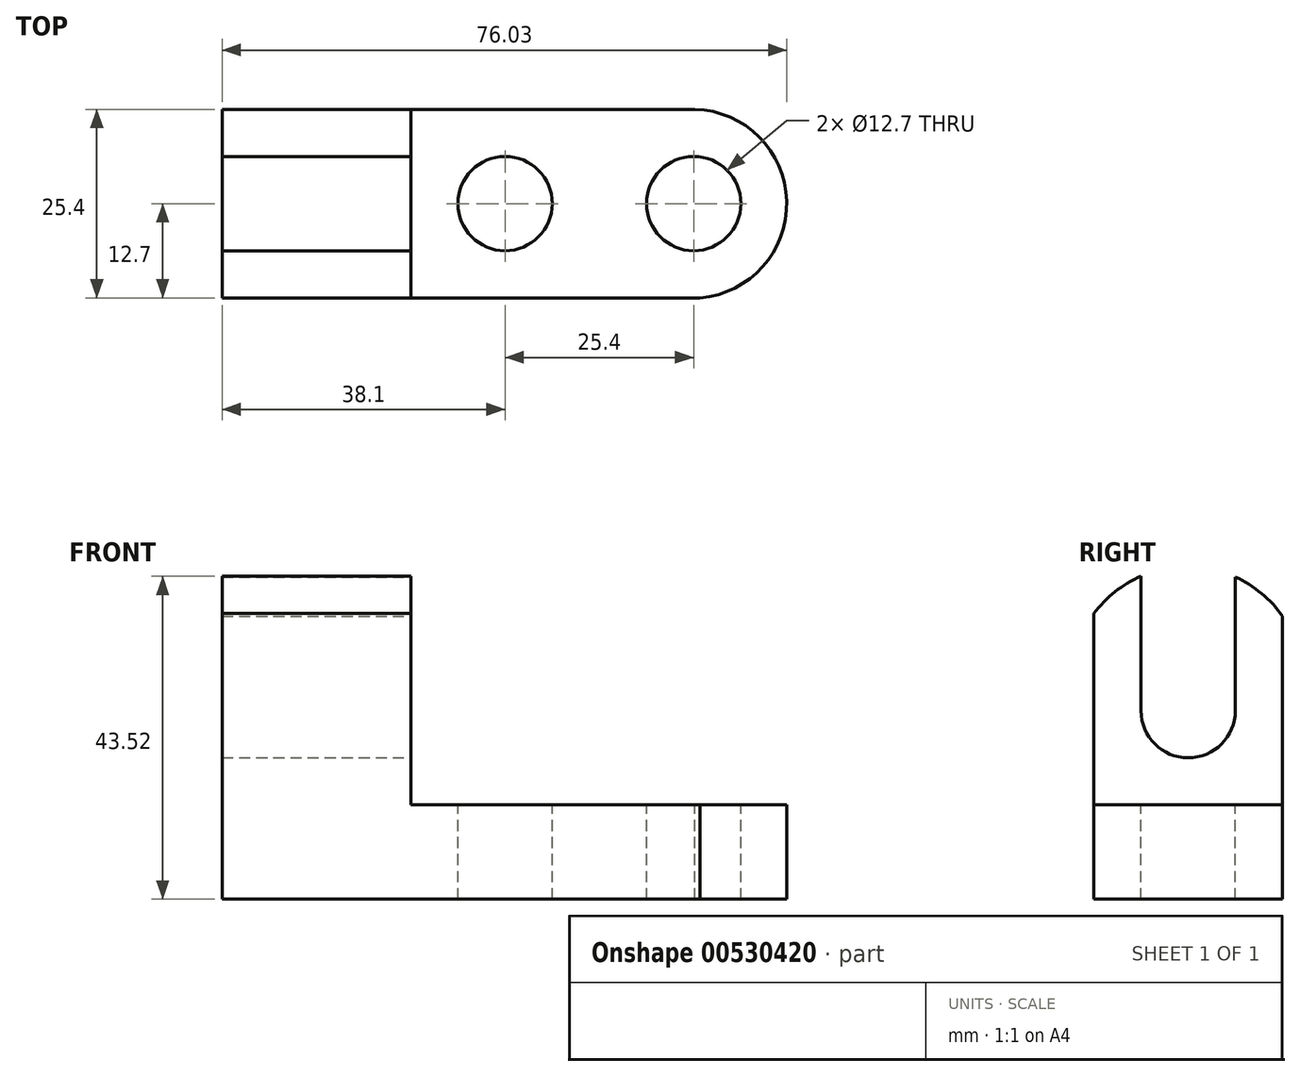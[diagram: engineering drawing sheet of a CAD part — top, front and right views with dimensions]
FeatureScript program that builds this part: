
annotation { "Feature Type Name" : "Feature", "Feature Type Description" : "" }
export const myFeature = defineFeature(function(context is Context, id is Id, definition is map)
    precondition{}
    {
        {
            var Q0;
            Q0=qCreatedBy(makeId("Front.planeOp"),FACE);
            var sketch = newSketch(context, id + "F0", { "sketchPlane" : qUnion([Q0])});
            skLineSegment(sketch, "E0", {"start": v(-76.2, 44.45) * mm, "end": v(-76.2, 0) * mm});
            skLineSegment(sketch, "E1", {"start": v(-76.2, 0) * mm, "end": v(0, 0) * mm});
            skLineSegment(sketch, "E2", {"start": v(-76.2, 44.45) * mm, "end": v(-50.8, 44.45) * mm});
            skLineSegment(sketch, "E3", {"start": v(-50.8, 44.45) * mm, "end": v(-50.8, 12.7) * mm});
            skLineSegment(sketch, "E4", {"start": v(-50.8, 12.7) * mm, "end": v(0, 12.7) * mm});
            skLineSegment(sketch, "E5", {"start": v(0, 12.7) * mm, "end": v(0, 0) * mm});
            skSolve(sketch);
        }
        {
            var Q0;
            Q0=makeQuery(id+"F0.imprint","IMPRINT",FACE,{"disambiguationData":[TD([[makeQuery(id+"F0.imprint","IMPRINT",EDGE,{"derivedFrom":sQuery(id+"F0.wireOp",EDGE,"E0")}),1.0]])]});
            extrude(context, id + "F1", {"entities" : qUnion([Q0]), "depth" : 25.4 * mm, "offsetDistance" : 25.4 * mm});
        }
        {
            var Q0;
            Q0=makeQuery(id+"F1.opExtrude","SWEPT_FACE",FACE,{"disambiguationData":[OSD([sQuery(id+"F0.wireOp",EDGE,"E4")])]});
            var sketch = newSketch(context, id + "F2", { "sketchPlane" : qUnion([Q0])});
            skCircle(sketch, "E6", {"center": v(-38.1, -12.7) * mm, "radius": 6.35 * mm});
            skCircle(sketch, "E7", {"center": v(-12.7, -12.7) * mm, "radius": 6.35 * mm});
            skSolve(sketch);
        }
        {
            var Q0;
            Q0=makeQuery(id+"F2.imprint","IMPRINT",FACE,{"disambiguationData":[TD([[makeQuery(id+"F2.imprint","IMPRINT",EDGE,{"derivedFrom":sQuery(id+"F2.wireOp",EDGE,"E6")}),1.0]])]});
            var Q1;
            Q1=makeQuery(id+"F2.imprint","IMPRINT",FACE,{"disambiguationData":[TD([[makeQuery(id+"F2.imprint","IMPRINT",EDGE,{"derivedFrom":sQuery(id+"F2.wireOp",EDGE,"E7")}),1.0]])]});
            extrude(context, id + "F3", {"entities" : qUnion([Q0, Q1]), "operationType" : NewBodyOperationType.REMOVE, "oppositeDirection" : true, "depth" : 25.4 * mm, "offsetDistance" : 25.4 * mm});
        }
        {
            var Q0;
            Q0=qCreatedBy(makeId("Right.planeOp"),FACE);
            var sketch = newSketch(context, id + "F4", { "sketchPlane" : qUnion([Q0])});
            skCircle(sketch, "E8", {"center": v(-12.7, 25.4) * mm, "radius": 6.35 * mm});
            skLineSegment(sketch, "E9", {"start": v(-19.05, 44.54) * mm, "end": v(-19.05, 25.4) * mm});
            skLineSegment(sketch, "E10", {"start": v(-6.35, 44.48) * mm, "end": v(-6.35, 25.4) * mm});
            skLineSegment(sketch, "E11", {"start": v(-19.05, 44.54) * mm, "end": v(-6.35, 44.48) * mm});
            skSolve(sketch);
        }
        {
            var Q0;
            {var subQ0=sQuery(id+"F4.wireOp",EDGE,"E8");var subQ1=makeQuery(id+"F4.imprint","INTERSECT",VERTEX,{"derivedFrom":[subQ0,sQuery(id+"F4.wireOp",EDGE,"E9")]});Q0=makeQuery(id+"F4.imprint","IMPRINT",FACE,{"disambiguationData":[TD([[makeQuery(id+"F4.imprint","IMPRINT",EDGE,{"disambiguationData":[TD([[subQ1,1.0]])],"derivedFrom":subQ0}),1.0]])]});}
            var Q1;
            {var subQ0=sQuery(id+"F4.wireOp",EDGE,"E9");Q1=makeQuery(id+"F4.imprint","IMPRINT",FACE,{"disambiguationData":[TD([[makeQuery(id+"F4.imprint","IMPRINT",EDGE,{"derivedFrom":subQ0}),1.0]])]});}
            extrude(context, id + "F5", {"entities" : qUnion([Q0, Q1]), "operationType" : NewBodyOperationType.REMOVE, "endBound" : BoundingType.THROUGH_ALL, "oppositeDirection" : true, "depth" : 25.4 * mm, "offsetDistance" : 25.4 * mm});
        }
        {
            var Q0;
            Q0=makeQuery(id+"F1.opExtrude","SWEPT_FACE",FACE,{"disambiguationData":[OSD([sQuery(id+"F0.wireOp",EDGE,"E3")])]});
            var sketch = newSketch(context, id + "F6", { "sketchPlane" : qUnion([Q0])});
            skArc(sketch, "E12", {"start": v(0, 38.14) * mm, "mid": v(-12.6, 44.8) * mm, "end": v(-25.4, 38.5) * mm});
            skSolve(sketch);
        }
        {
            var Q0;
            {var subQ0=sQuery(id+"F6.wireOp",EDGE,"E12");var subQ1=sQuery(id+"F0.wireOp",EDGE,"E3");var subQ2=makeQuery(id+"F1.opExtrude","CAP_EDGE",EDGE,{"disambiguationData":[OSD([subQ1])],"isStart":false});var subQ3=makeQuery(id+"F6.imprint","INTERSECT",VERTEX,{"derivedFrom":[subQ2,subQ0]});Q0=makeQuery(id+"F6.imprint","IMPRINT",FACE,{"disambiguationData":[TD([[makeQuery(id+"F6.imprint","IMPRINT",EDGE,{"disambiguationData":[TD([[subQ3,1.0]])],"derivedFrom":subQ0}),-1.0]])]});}
            var Q1;
            {var subQ0=sQuery(id+"F6.wireOp",EDGE,"E12");var subQ1=sQuery(id+"F0.wireOp",EDGE,"E3");var subQ2=makeQuery(id+"F1.opExtrude","CAP_EDGE",EDGE,{"disambiguationData":[OSD([subQ1])],"isStart":true});var subQ3=makeQuery(id+"F6.imprint","INTERSECT",VERTEX,{"derivedFrom":[subQ2,subQ0]});Q1=makeQuery(id+"F6.imprint","IMPRINT",FACE,{"disambiguationData":[TD([[makeQuery(id+"F6.imprint","IMPRINT",EDGE,{"disambiguationData":[TD([[subQ3,-1.0]])],"derivedFrom":subQ0}),-1.0]])]});}
            extrude(context, id + "F7", {"entities" : qUnion([Q0, Q1]), "operationType" : NewBodyOperationType.REMOVE, "endBound" : BoundingType.THROUGH_ALL, "oppositeDirection" : true, "depth" : 25.4 * mm, "offsetDistance" : 25.4 * mm});
        }
        {
            var Q0;
            Q0=makeQuery(id+"F1.opExtrude","SWEPT_FACE",FACE,{"disambiguationData":[OSD([sQuery(id+"F0.wireOp",EDGE,"E4")])]});
            var sketch = newSketch(context, id + "F8", { "sketchPlane" : qUnion([Q0])});
            skArc(sketch, "E13", {"start": v(-11.82, -25.4) * mm, "mid": v(-0.19, -12) * mm, "end": v(-13.25, 0) * mm});
            skSolve(sketch);
        }
        {
            var Q0;
            {var subQ1=sQuery(id+"F0.wireOp",EDGE,"E4");var subQ6=makeQuery(id+"F1.opExtrude","SWEPT_EDGE",EDGE,{"disambiguationData":[OSD([subQ1,sQuery(id+"F0.wireOp",EDGE,"E5")])]});Q0=makeQuery(id+"F8.imprint","IMPRINT",FACE,{"disambiguationData":[TD([[makeQuery(id+"F8.imprint","IMPRINT",EDGE,{"derivedFrom":subQ6}),1.0]])]});}
            extrude(context, id + "F9", {"entities" : qUnion([Q0]), "operationType" : NewBodyOperationType.REMOVE, "endBound" : BoundingType.THROUGH_ALL, "oppositeDirection" : true, "depth" : 25.4 * mm, "offsetDistance" : 25.4 * mm});
        }
    });
